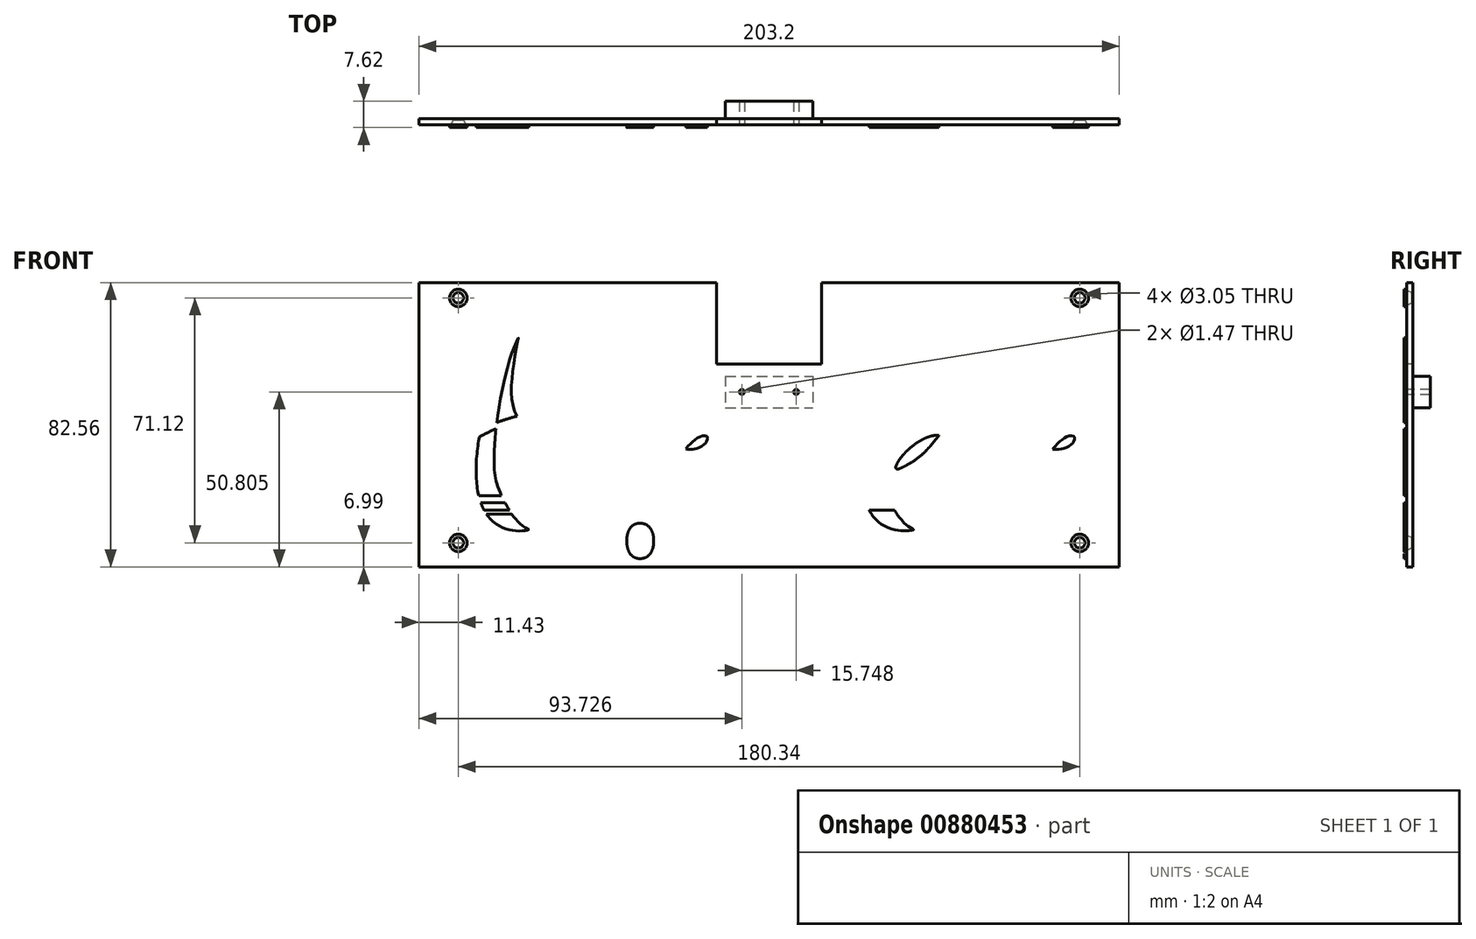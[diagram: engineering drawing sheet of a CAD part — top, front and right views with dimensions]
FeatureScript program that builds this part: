
annotation { "Feature Type Name" : "Feature", "Feature Type Description" : "" }
export const myFeature = defineFeature(function(context is Context, id is Id, definition is map)
    precondition{}
    {
        {
            var Q0;
            Q0=qCreatedBy(makeId("Front.planeOp"),FACE);
            var sketch = newSketch(context, id + "F0", { "sketchPlane" : qUnion([Q0])});
            skLineSegment(sketch, "E0.bottom", {"start": v(-101.6, 41.27) * mm, "end": v(101.6, 41.27) * mm});
            skLineSegment(sketch, "E0.top", {"start": v(-101.6, -41.27) * mm, "end": v(101.6, -41.27) * mm});
            skLineSegment(sketch, "E0.left", {"start": v(-101.6, 41.27) * mm, "end": v(-101.6, -41.27) * mm});
            skLineSegment(sketch, "E0.right", {"start": v(101.6, 41.27) * mm, "end": v(101.6, -41.27) * mm});
            skPoint(sketch, "E0.middle", {"position": v(0, 0) * mm});
            skSolve(sketch);
        }
        {
            var Q0;
            Q0 = qSketchRegion(id + "F0", true);
            extrude(context, id + "F1", {"entities" : qUnion([Q0]), "depth" : 2.54 * mm, "offsetDistance" : 25.4 * mm});
        }
        {
            var Q0;
            Q0=makeQuery(id+"F1.opExtrude","CAP_FACE",FACE,{"disambiguationData":[OSD([sQuery(id+"F0.wireOp",EDGE,"E0.bottom"),sQuery(id+"F0.wireOp",EDGE,"E0.top"),sQuery(id+"F0.wireOp",EDGE,"E0.left"),sQuery(id+"F0.wireOp",EDGE,"E0.right")])],"isStart":false});
            var sketch = newSketch(context, id + "F2", { "sketchPlane" : qUnion([Q0])});
            skLineSegment(sketch, "E1.bottom", {"start": v(-99.06, 41.27) * mm, "end": v(-82.55, 41.27) * mm});
            skLineSegment(sketch, "E1.top", {"start": v(-99.06, 32.38) * mm, "end": v(-82.55, 32.38) * mm});
            skLineSegment(sketch, "E1.left", {"start": v(-99.06, 41.27) * mm, "end": v(-99.06, 32.38) * mm});
            skLineSegment(sketch, "E1.right", {"start": v(-82.55, 41.27) * mm, "end": v(-82.55, 32.38) * mm});
            skLineSegment(sketch, "E2.bottom", {"start": v(99.06, 41.27) * mm, "end": v(82.55, 41.27) * mm});
            skLineSegment(sketch, "E2.top", {"start": v(99.06, 32.38) * mm, "end": v(82.55, 32.38) * mm});
            skLineSegment(sketch, "E2.left", {"start": v(99.06, 41.27) * mm, "end": v(99.06, 32.38) * mm});
            skLineSegment(sketch, "E2.right", {"start": v(82.55, 41.27) * mm, "end": v(82.55, 32.38) * mm});
            skLineSegment(sketch, "E3.bottom", {"start": v(99.06, -38.73) * mm, "end": v(82.55, -38.73) * mm});
            skLineSegment(sketch, "E3.top", {"start": v(99.06, -29.84) * mm, "end": v(82.55, -29.84) * mm});
            skLineSegment(sketch, "E3.left", {"start": v(99.06, -38.73) * mm, "end": v(99.06, -29.84) * mm});
            skLineSegment(sketch, "E3.right", {"start": v(82.55, -38.74) * mm, "end": v(82.55, -29.85) * mm});
            skLineSegment(sketch, "E4.bottom", {"start": v(-99.06, -38.74) * mm, "end": v(-82.55, -38.74) * mm});
            skLineSegment(sketch, "E4.top", {"start": v(-99.06, -29.85) * mm, "end": v(-82.55, -29.85) * mm});
            skLineSegment(sketch, "E4.left", {"start": v(-99.06, -38.74) * mm, "end": v(-99.06, -29.85) * mm});
            skLineSegment(sketch, "E4.right", {"start": v(-82.55, -38.74) * mm, "end": v(-82.55, -29.85) * mm});
            skPoint(sketch, "E5", {"position": v(-90.17, 36.83) * mm});
            skPoint(sketch, "E5.positionSnap0", {"position": v(-82.55, 36.83) * mm});
            skPoint(sketch, "E6", {"position": v(-90.17, -34.3) * mm});
            skPoint(sketch, "E6.positionSnap0", {"position": v(-82.55, -34.3) * mm});
            skPoint(sketch, "E7", {"position": v(90.17, -34.3) * mm});
            skPoint(sketch, "E8", {"position": v(90.17, 36.83) * mm});
            skPoint(sketch, "E8.positionSnap0", {"position": v(82.55, 36.83) * mm});
            skLineSegment(sketch, "E9.bottom", {"start": v(-15.24, 41.27) * mm, "end": v(15.24, 41.27) * mm});
            skLineSegment(sketch, "E9.top", {"start": v(-15.24, 17.65) * mm, "end": v(15.24, 17.65) * mm});
            skLineSegment(sketch, "E9.left", {"start": v(-15.24, 41.27) * mm, "end": v(-15.24, 17.65) * mm});
            skLineSegment(sketch, "E9.right", {"start": v(15.24, 41.27) * mm, "end": v(15.24, 17.65) * mm});
            skPoint(sketch, "E9.middle", {"position": v(0, 29.46) * mm});
            skLineSegment(sketch, "E10.bottom", {"start": v(-12.7, 17.65) * mm, "end": v(12.7, 17.65) * mm});
            skLineSegment(sketch, "E10.top", {"start": v(-12.7, 4.95) * mm, "end": v(12.7, 4.95) * mm});
            skLineSegment(sketch, "E10.left", {"start": v(-12.7, 17.65) * mm, "end": v(-12.7, 4.95) * mm});
            skLineSegment(sketch, "E10.right", {"start": v(12.7, 17.65) * mm, "end": v(12.7, 4.95) * mm});
            skPoint(sketch, "E10.middle", {"position": v(0, 11.3) * mm});
            skLineSegment(sketch, "E11", {"start": v(-12.7, 9.52) * mm, "end": v(12.7, 9.52) * mm, "construction": true});
            skPoint(sketch, "E12", {"position": v(0, 9.52) * mm});
            skPoint(sketch, "E13", {"position": v(-7.87, 9.52) * mm});
            skPoint(sketch, "E14", {"position": v(7.87, 9.52) * mm});
            skLineSegment(sketch, "E15", {"start": v(-12.7, 14.1) * mm, "end": v(12.7, 14.1) * mm});
            skSolve(sketch);
        }
        {
            var Q0;
            Q0=sQuery(id+"F2.wireOp",VERTEX,"E5");
            var Q1;
            Q1=sQuery(id+"F2.wireOp",VERTEX,"E6");
            var Q2;
            Q2=sQuery(id+"F2.wireOp",VERTEX,"E7");
            var Q3;
            Q3=sQuery(id+"F2.wireOp",VERTEX,"E8");
            var Q4;
            Q4=makeQuery(id+"F1.opExtrude","SWEPT_BODY",BODY,{"disambiguationData":[OSD([sQuery(id+"F0.wireOp",EDGE,"E0.bottom"),sQuery(id+"F0.wireOp",EDGE,"E0.top"),sQuery(id+"F0.wireOp",EDGE,"E0.left"),sQuery(id+"F0.wireOp",EDGE,"E0.right")])]});
            hole(context, id + "F3", {"style" : HoleStyle.C_SINK, "endStyle" : HoleEndStyle.THROUGH, "holeDiameter" : 3.05 * mm, "cSinkDiameter" : 5.08 * mm, "cSinkAngle" : 49 * degree, "majorDiameter" : 6.35 * mm, "isTappedThrough" : true, "tappedDepth" : 12.7 * mm, "tapClearance" : 3, "locations" : qUnion([Q0, Q1, Q2, Q3]), "scope" : qUnion([Q4])});
        }
        {
            var Q0;
            Q0=makeQuery(id+"F2.imprint","IMPRINT",FACE,{"disambiguationData":[TD([[makeQuery(id+"F2.imprint","IMPRINT",EDGE,{"derivedFrom":sQuery(id+"F2.wireOp",EDGE,"rZs2VQ7l-vhOc-SYSJ-Oo8c-zqr43qeV2ue8.bottom")}),-1.0]])]});
            var Q1;
            Q1=makeQuery(id+"F2.imprint","IMPRINT",FACE,{"disambiguationData":[TD([[makeQuery(id+"F2.imprint","IMPRINT",EDGE,{"derivedFrom":sQuery(id+"F2.wireOp",EDGE,"E9.bottom")}),-1.0]])]});
            extrude(context, id + "F4", {"entities" : qUnion([Q0, Q1]), "operationType" : NewBodyOperationType.REMOVE, "oppositeDirection" : true, "depth" : 25.4 * mm, "offsetDistance" : 25.4 * mm});
        }
        {
            var Q0;
            {var subQ0=sQuery(id+"F2.wireOp",EDGE,"E10.top");Q0=makeQuery(id+"F2.imprint","IMPRINT",FACE,{"disambiguationData":[TD([[makeQuery(id+"F2.imprint","IMPRINT",EDGE,{"derivedFrom":subQ0}),1.0]])]});}
            extrude(context, id + "F5", {"entities" : qUnion([Q0]), "operationType" : NewBodyOperationType.ADD, "oppositeDirection" : true, "depth" : 7.62 * mm, "offsetDistance" : 25.4 * mm});
        }
        {
            var Q0;
            Q0=sQuery(id+"F2.wireOp",VERTEX,"E13");
            var Q1;
            Q1=sQuery(id+"F2.wireOp",VERTEX,"E14");
            var Q2;
            Q2=makeQuery(id+"F1.opExtrude","SWEPT_BODY",BODY,{"disambiguationData":[OSD([sQuery(id+"F0.wireOp",EDGE,"E0.bottom"),sQuery(id+"F0.wireOp",EDGE,"E0.top"),sQuery(id+"F0.wireOp",EDGE,"E0.left"),sQuery(id+"F0.wireOp",EDGE,"E0.right")])]});
            hole(context, id + "F6", {"style" : HoleStyle.SIMPLE, "endStyle" : HoleEndStyle.BLIND, "holeDiameter" : 1.47 * mm, "majorDiameter" : 6.35 * mm, "holeDepth" : 10.16 * mm, "isTappedThrough" : true, "tappedDepth" : 12.7 * mm, "tapClearance" : 3, "locations" : qUnion([Q0, Q1]), "scope" : qUnion([Q2])});
        }
        {
            var Q0;
            Q0=makeQuery(id+"F1.opExtrude","CAP_FACE",FACE,{"disambiguationData":[OSD([sQuery(id+"F0.wireOp",EDGE,"E0.bottom"),sQuery(id+"F0.wireOp",EDGE,"E0.top"),sQuery(id+"F0.wireOp",EDGE,"E0.left"),sQuery(id+"F0.wireOp",EDGE,"E0.right")])],"isStart":false});
            var sketch = newSketch(context, id + "F7", { "sketchPlane" : qUnion([Q0])});
            skLineSegment(sketch, "E16.bottom", {"start": v(-99.39, -20.57) * mm, "end": v(98.42, -20.57) * mm});
            skLineSegment(sketch, "E16.top", {"start": v(-99.39, -22.6) * mm, "end": v(98.42, -22.6) * mm});
            skLineSegment(sketch, "E16.left", {"start": v(-99.39, -20.57) * mm, "end": v(-99.39, -22.6) * mm});
            skLineSegment(sketch, "E16.right", {"start": v(98.42, -20.57) * mm, "end": v(98.42, -22.6) * mm});
            skLineSegment(sketch, "E17.bottom", {"start": v(-99.39, -24.83) * mm, "end": v(98.42, -24.83) * mm});
            skLineSegment(sketch, "E17.top", {"start": v(-99.39, -25.88) * mm, "end": v(98.42, -25.88) * mm});
            skLineSegment(sketch, "E17.left", {"start": v(-99.39, -24.83) * mm, "end": v(-99.39, -25.88) * mm});
            skLineSegment(sketch, "E17.right", {"start": v(98.42, -24.83) * mm, "end": v(98.42, -25.88) * mm});
            skFitSpline(sketch, "E18", {"points": [v(-99.39, -13.37) * mm, v(-98.49, -14.18) * mm, v(-98.4, -14.28) * mm, v(-98.28, -14.17) * mm, v(-96.93, -12.76) * mm, v(-95.43, -11.38) * mm, v(-93.7, -9.92) * mm, v(-91.22, -7.99) * mm, v(-88.97, -6.44) * mm, v(-86.37, -4.82) * mm, v(-84.08, -3.54) * mm, v(-79.14, -1.1) * mm, v(-76.01, 0.1) * mm, v(-72.39, 1.31) * mm, v(-68.08, 2.4) * mm, v(-64.6, 3.07) * mm, v(-61.72, 3.46) * mm, v(-58.9, 3.7) * mm, v(-56.18, 3.84) * mm, v(-52.18, 3.75) * mm, v(-47.22, 3.4) * mm, v(-44.4, 3) * mm, v(-41.38, 2.42) * mm, v(-39.4, 2) * mm, v(-39.54, 2.08) * mm, v(-40.44, 2.32) * mm, v(-42.26, 2.75) * mm, v(-45.54, 3.4) * mm, v(-47.8, 3.78) * mm, v(-50.36, 4.1) * mm, v(-52.71, 4.33) * mm, v(-55.15, 4.46) * mm, v(-57.94, 4.5) * mm, v(-60.7, 4.44) * mm, v(-63.58, 4.22) * mm, v(-67, 3.8) * mm, v(-69.33, 3.38) * mm, v(-71.76, 2.87) * mm, v(-74.4, 2.15) * mm, v(-76.35, 1.56) * mm, v(-78, 1.02) * mm, v(-79, 0.66) * mm, v(-83.6, -1.22) * mm, v(-86.89, -2.84) * mm, v(-89.86, -4.53) * mm, v(-92.19, -5.98) * mm, v(-94.38, -7.5) * mm, v(-96.5, -9.12) * mm, v(-98.21, -10.58) * mm, v(-99.5, -11.75) * mm, v(-100.21, -12.45) * mm, v(-100.24, -12.51) * mm, v(-100.18, -12.6) * mm, v(-99.72, -13.04) * mm, v(-99.39, -13.37) * mm]});
            skFitSpline(sketch, "E19", {"points": [v(-69.85, -30.36) * mm, v(-69.72, -30.45) * mm, v(-69.94, -30.55) * mm, v(-70.41, -30.65) * mm, v(-70.92, -30.73) * mm, v(-71.77, -30.84) * mm, v(-72.94, -30.84) * mm, v(-74.08, -30.7) * mm, v(-75.15, -30.53) * mm, v(-76.3, -30.22) * mm, v(-77.61, -29.7) * mm, v(-78.84, -29.04) * mm, v(-80.19, -28.03) * mm, v(-81.17, -27.03) * mm, v(-81.85, -26.16) * mm, v(-82.41, -25.28) * mm, v(-82.99, -24.23) * mm, v(-83.45, -23.13) * mm, v(-83.94, -21.79) * mm, v(-84.38, -19.96) * mm, v(-84.73, -17.88) * mm, v(-84.92, -15.83) * mm, v(-85, -13.09) * mm, v(-84.91, -10.36) * mm, v(-84.7, -7.94) * mm, v(-84.4, -5.56) * mm, v(-84.13, -3.82) * mm, v(-83.72, -1.92) * mm, v(-83.24, 0.53) * mm, v(-82.35, 3.98) * mm, v(-81.4, 7.25) * mm, v(-80.28, 10.95) * mm, v(-78.6, 15.64) * mm, v(-76.82, 20.12) * mm, v(-75.21, 23.83) * mm, v(-73.83, 26.82) * mm, v(-72.43, 29.66) * mm, v(-71.33, 31.65) * mm, v(-71.2, 31.83) * mm, v(-70.88, 31.85) * mm, v(-70.46, 31.82) * mm, v(-69.92, 31.64) * mm, v(-69.72, 31.52) * mm, v(-69.77, 31.22) * mm, v(-70.28, 29.04) * mm, v(-70.9, 26.38) * mm, v(-71.46, 23.53) * mm, v(-72.11, 19.9) * mm, v(-72.62, 16.3) * mm, v(-72.96, 13.2) * mm, v(-73.13, 11.06) * mm, v(-73.2, 8.7) * mm, v(-72.96, 6.27) * mm, v(-72.39, 4.05) * mm, v(-72.03, 3.01) * mm, v(-71.55, 2.04) * mm, v(-71.01, 1.27) * mm, v(-70.16, 0.39) * mm, v(-69.38, -0.13) * mm, v(-68.74, -0.5) * mm, v(-68.6, -0.57) * mm, v(-68.78, -0.6) * mm, v(-69.3, -0.6) * mm, v(-69.86, -0.5) * mm, v(-70.5, -0.21) * mm, v(-71.05, 0.16) * mm, v(-71.83, 0.81) * mm, v(-72.16, 1.17) * mm, v(-72.64, 1.79) * mm, v(-73.15, 2.6) * mm, v(-73.8, 3.88) * mm, v(-74.19, 5.1) * mm, v(-74.56, 6.8) * mm, v(-74.73, 8.53) * mm, v(-74.78, 10.39) * mm, v(-74.68, 12.54) * mm, v(-74.5, 14.34) * mm, v(-74.2, 16.97) * mm, v(-73.87, 19.16) * mm, v(-73.45, 21.5) * mm, v(-73.03, 23.66) * mm, v(-72.73, 25.04) * mm, v(-72.7, 25.22) * mm, v(-72.86, 25.01) * mm, v(-73.28, 24.03) * mm, v(-74.08, 22.26) * mm, v(-74.63, 21) * mm, v(-75.1, 19.38) * mm, v(-75.94, 16.33) * mm, v(-76.99, 12.07) * mm, v(-77.88, 7.83) * mm, v(-78.47, 4.47) * mm, v(-78.84, 1.84) * mm, v(-79.1, 0.05) * mm, v(-79.33, -1.92) * mm, v(-79.51, -4.07) * mm, v(-79.7, -7.13) * mm, v(-79.79, -9.63) * mm, v(-79.79, -12.03) * mm, v(-79.54, -14.42) * mm, v(-79.14, -16.53) * mm, v(-78.2, -19.32) * mm, v(-77.03, -21.86) * mm, v(-75.64, -24.3) * mm, v(-74.49, -26.1) * mm, v(-73.94, -26.87) * mm, v(-73.18, -27.76) * mm, v(-72.52, -28.47) * mm, v(-71.59, -29.32) * mm, v(-70.71, -29.93) * mm, v(-70.12, -30.24) * mm, v(-69.85, -30.36) * mm]});
            skFitSpline(sketch, "E20", {"points": [v(41.78, -30.33) * mm, v(42.01, -30.45) * mm, v(41.87, -30.52) * mm, v(41.45, -30.64) * mm, v(40.67, -30.74) * mm, v(39.96, -30.8) * mm, v(39.22, -30.81) * mm, v(38.16, -30.78) * mm, v(37.1, -30.63) * mm, v(35.95, -30.38) * mm, v(34.5, -29.89) * mm, v(32.96, -29.07) * mm, v(31.8, -28.25) * mm, v(30.75, -27.2) * mm, v(29.85, -26.09) * mm, v(29.32, -25.23) * mm, v(28.77, -24.25) * mm, v(28.19, -22.93) * mm, v(27.75, -21.63) * mm, v(27.3, -19.79) * mm, v(27.06, -18.22) * mm, v(26.84, -16.17) * mm, v(26.75, -14.13) * mm, v(26.75, -11.98) * mm, v(26.84, -10) * mm, v(27.06, -7.76) * mm, v(27.38, -5.27) * mm, v(27.79, -2.84) * mm, v(28.33, -0.38) * mm, v(28.9, 2.15) * mm, v(29.9, 5.76) * mm, v(31.53, 11.05) * mm, v(33, 15.33) * mm, v(34.8, 19.85) * mm, v(36.6, 24.06) * mm, v(38.29, 27.6) * mm, v(40.44, 31.72) * mm, v(40.53, 31.84) * mm, v(40.75, 31.9) * mm, v(41.11, 31.84) * mm, v(41.55, 31.73) * mm, v(41.98, 31.5) * mm, v(42.03, 31.46) * mm, v(41.95, 31.3) * mm, v(41.08, 29.61) * mm, v(40.26, 27.95) * mm, v(39.36, 26.06) * mm, v(37.5, 21.88) * mm, v(37.02, 20.76) * mm, v(35.83, 16.46) * mm, v(34.55, 11.25) * mm, v(33.75, 7.34) * mm, v(32.83, 1.74) * mm, v(32.4, -2.34) * mm, v(32.01, -6.96) * mm, v(31.94, -9.98) * mm, v(32.1, -13.2) * mm, v(32.48, -15.89) * mm, v(33.23, -18.56) * mm, v(34.02, -20.36) * mm, v(34.8, -21.88) * mm, v(35.87, -23.96) * mm, v(37.3, -26.14) * mm, v(38.22, -27.37) * mm, v(39.27, -28.52) * mm, v(40, -29.23) * mm, v(40.56, -29.65) * mm, v(41.11, -30) * mm, v(41.78, -30.33) * mm]});
            skFitSpline(sketch, "E21", {"points": [v(-77.34, -13.2) * mm, v(-77.53, -12.77) * mm, v(-77.62, -12.5) * mm, v(-77.54, -12.07) * mm, v(-77.01, -11.44) * mm, v(-75.8, -10.4) * mm, v(-75.03, -9.75) * mm, v(-74.83, -9.6) * mm, v(-73.77, -8.2) * mm, v(-71.45, -4.88) * mm, v(-70.26, -3.1) * mm, v(-69.98, -2.85) * mm, v(-69.54, -2.8) * mm, v(-69, -2.94) * mm, v(-68.48, -3.33) * mm, v(-68.44, -3.72) * mm, v(-68.68, -4.1) * mm, v(-70.07, -5.64) * mm, v(-70.96, -6.84) * mm, v(-71.37, -7.37) * mm, v(-71.5, -7.58) * mm, v(-71.2, -7.47) * mm, v(-70.86, -7.23) * mm, v(-68.87, -6.07) * mm, v(-67.23, -5.13) * mm, v(-64.84, -3.82) * mm, v(-62.8, -2.83) * mm, v(-61.57, -2.35) * mm, v(-61, -2.32) * mm, v(-60.6, -2.61) * mm, v(-60.4, -2.99) * mm, v(-60.58, -3.33) * mm, v(-61, -3.83) * mm, v(-61.98, -4.8) * mm, v(-63.5, -6.42) * mm, v(-64.58, -7.67) * mm, v(-65.75, -9.14) * mm, v(-66.83, -10.76) * mm, v(-67.34, -11.81) * mm, v(-67.46, -12.5) * mm, v(-67.32, -13.07) * mm, v(-66.74, -13.42) * mm, v(-65.92, -13.48) * mm, v(-64.01, -13.2) * mm, v(-61.05, -12) * mm, v(-58.33, -10.55) * mm, v(-57.1, -9.75) * mm, v(-55.38, -8.53) * mm, v(-55.05, -8.32) * mm, v(-55.6, -9.43) * mm, v(-56.18, -9.65) * mm, v(-56.63, -9.87) * mm, v(-57.53, -10.48) * mm, v(-58.37, -11.01) * mm, v(-59.95, -11.92) * mm, v(-61.58, -12.69) * mm, v(-63.45, -13.4) * mm, v(-65.27, -13.9) * mm, v(-66.76, -14.12) * mm, v(-68.4, -14.12) * mm, v(-69.33, -13.96) * mm, v(-69.81, -13.74) * mm, v(-70.04, -13.26) * mm, v(-69.92, -12.5) * mm, v(-69.4, -11.45) * mm, v(-67.66, -9.18) * mm, v(-65.97, -7.16) * mm, v(-64.92, -5.92) * mm, v(-64.04, -4.74) * mm, v(-63.77, -4.17) * mm, v(-63.95, -3.95) * mm, v(-64.34, -4.04) * mm, v(-65.94, -4.84) * mm, v(-69.02, -6.6) * mm, v(-71.16, -7.98) * mm, v(-71.95, -8.55) * mm, v(-72.65, -9.2) * mm, v(-73.73, -10.43) * mm, v(-74.95, -11.87) * mm, v(-75.92, -12.96) * mm, v(-76.6, -13.62) * mm, v(-76.92, -13.68) * mm, v(-77.2, -13.5) * mm, v(-77.34, -13.2) * mm]});
            skFitSpline(sketch, "E22", {"points": [v(-45.1, -5.77) * mm, v(-45.2, -6) * mm, v(-44.96, -6.03) * mm, v(-44.25, -5.67) * mm, v(-43.46, -5.18) * mm, v(-43.1, -4.6) * mm, v(-43.05, -3.91) * mm, v(-43.43, -3.21) * mm, v(-44.33, -2.81) * mm, v(-45.5, -2.67) * mm, v(-46.88, -2.81) * mm, v(-48.87, -3.5) * mm, v(-50.67, -4.32) * mm, v(-52.34, -5.33) * mm, v(-53.65, -6.34) * mm, v(-54.84, -7.47) * mm, v(-55.5, -8.23) * mm, v(-55.91, -8.79) * mm, v(-56.45, -9.56) * mm, v(-56.78, -10.3) * mm, v(-57.02, -11.04) * mm, v(-57.06, -11.84) * mm, v(-56.86, -12.53) * mm, v(-56.36, -13.1) * mm, v(-55.6, -13.47) * mm, v(-54.41, -13.77) * mm, v(-52.9, -13.83) * mm, v(-51.33, -13.73) * mm, v(-49.3, -13.27) * mm, v(-47.12, -12.5) * mm, v(-44.79, -11.41) * mm, v(-41.78, -9.57) * mm, v(-39.31, -7.84) * mm, v(-38.14, -7) * mm, v(-37.84, -6.7) * mm, v(-37.93, -6.5) * mm, v(-38.42, -6.57) * mm, v(-38.75, -6.84) * mm, v(-39.98, -7.77) * mm, v(-41.5, -8.9) * mm, v(-43.3, -10.06) * mm, v(-44.77, -10.9) * mm, v(-46.71, -11.8) * mm, v(-48.57, -12.54) * mm, v(-50.37, -13.02) * mm, v(-52.07, -13.07) * mm, v(-53.32, -12.67) * mm, v(-54.12, -11.89) * mm, v(-54.25, -10.7) * mm, v(-54.08, -9.56) * mm, v(-53.56, -8.1) * mm, v(-52.72, -6.76) * mm, v(-51.58, -5.55) * mm, v(-50.45, -4.74) * mm, v(-49.04, -4.12) * mm, v(-47.7, -3.86) * mm, v(-46.31, -3.93) * mm, v(-45.54, -4.3) * mm, v(-45.08, -4.85) * mm, v(-45.1, -5.77) * mm]});
            skFitSpline(sketch, "E23", {"points": [v(-33.43, -3.72) * mm, v(-33.26, -3.56) * mm, v(-33.06, -3.13) * mm, v(-33.16, -3.03) * mm, v(-33.44, -3) * mm, v(-34.05, -3.1) * mm, v(-35.07, -3.4) * mm, v(-35.43, -3.53) * mm, v(-35.62, -3.6) * mm, v(-35.98, -3.92) * mm, v(-37.4, -5.44) * mm, v(-38.24, -6.35) * mm, v(-39.94, -8.42) * mm, v(-40.66, -9.4) * mm, v(-41.4, -10.53) * mm, v(-41.77, -11.37) * mm, v(-41.78, -12.32) * mm, v(-41.32, -12.87) * mm, v(-40.47, -13.32) * mm, v(-39.31, -13.48) * mm, v(-37.66, -13.47) * mm, v(-35.8, -13.16) * mm, v(-33.52, -12.46) * mm, v(-31.34, -11.43) * mm, v(-28.7, -9.95) * mm, v(-26.52, -8.45) * mm, v(-26.38, -8.32) * mm, v(-26.68, -8.43) * mm, v(-27.3, -8.65) * mm, v(-27.83, -8.93) * mm, v(-28.59, -9.42) * mm, v(-30.11, -10.33) * mm, v(-32.2, -11.41) * mm, v(-34.12, -12.23) * mm, v(-35.79, -12.7) * mm, v(-37.32, -12.83) * mm, v(-38.42, -12.54) * mm, v(-38.84, -11.93) * mm, v(-38.63, -10.76) * mm, v(-37.74, -9.12) * mm, v(-36.31, -7.08) * mm, v(-34.58, -5) * mm, v(-33.43, -3.72) * mm]});
            skFitSpline(sketch, "E24", {"points": [v(-30.4, 4.17) * mm, v(-30, 4.35) * mm, v(-29.4, 4.52) * mm, v(-28.83, 4.53) * mm, v(-28.35, 4.44) * mm, v(-28.14, 4.22) * mm, v(-28.06, 3.85) * mm, v(-28.15, 3.53) * mm, v(-28.47, 3.05) * mm, v(-28.52, 3) * mm, v(-29, 2.58) * mm, v(-29.04, 2.56) * mm, v(-29.53, 2.31) * mm, v(-29.6, 2.28) * mm, v(-30.2, 2.14) * mm, v(-30.8, 2.16) * mm, v(-31.21, 2.3) * mm, v(-31.38, 2.61) * mm, v(-31.33, 3.02) * mm, v(-31.19, 3.37) * mm, v(-30.97, 3.67) * mm, v(-30.62, 4.02) * mm, v(-30.4, 4.17) * mm]});
            skFitSpline(sketch, "E25", {"points": [v(-24.17, -7.05) * mm, v(-23.92, -6.7) * mm, v(-23.16, -5.85) * mm, v(-21.9, -4.66) * mm, v(-20.42, -3.62) * mm, v(-19.14, -3.2) * mm, v(-18.3, -3.23) * mm, v(-17.91, -3.57) * mm, v(-17.9, -4.05) * mm, v(-18.05, -4.72) * mm, v(-18.48, -5.36) * mm, v(-19.33, -6.08) * mm, v(-20.47, -6.7) * mm, v(-21.42, -7) * mm, v(-22.29, -7.14) * mm, v(-23.47, -7.18) * mm, v(-24.17, -7.05) * mm]});
            skFitSpline(sketch, "E26", {"points": [v(-24.52, -7.58) * mm, v(-24.33, -7.59) * mm, v(-22.9, -7.58) * mm, v(-19.62, -7) * mm, v(-17.33, -5.96) * mm, v(-15.87, -4.57) * mm, v(-15.5, -3.6) * mm, v(-15.85, -2.95) * mm, v(-16.86, -2.65) * mm, v(-18.48, -2.7) * mm, v(-20.68, -3.33) * mm, v(-23.37, -4.7) * mm, v(-25.9, -6.67) * mm, v(-27.47, -8.55) * mm, v(-28.4, -10.3) * mm, v(-28.7, -11.58) * mm, v(-28.46, -12.77) * mm, v(-27.2, -13.67) * mm, v(-25.78, -13.9) * mm, v(-23.09, -13.77) * mm, v(-20.54, -13.21) * mm, v(-17.52, -12.15) * mm, v(-14.42, -10.63) * mm, v(-10.85, -8.25) * mm, v(-10.75, -8.16) * mm, v(-10.54, -7.63) * mm, v(-10.78, -7.63) * mm, v(-11.45, -8.07) * mm, v(-12.74, -9.04) * mm, v(-15.12, -10.48) * mm, v(-17.29, -11.54) * mm, v(-19.65, -12.4) * mm, v(-21.63, -12.85) * mm, v(-23.67, -12.89) * mm, v(-25.2, -12.34) * mm, v(-25.68, -11.21) * mm, v(-25.62, -10.03) * mm, v(-25.16, -8.7) * mm, v(-24.6, -7.7) * mm, v(-24.52, -7.58) * mm]});
            skFitSpline(sketch, "E27", {"points": [v(-8.84, -7.46) * mm, v(-9.05, -7.58) * mm, v(-9, -7.4) * mm, v(-8.36, -6.57) * mm, v(-7.25, -5.22) * mm, v(-6.24, -4.06) * mm, v(-6.03, -3.76) * mm, v(-6, -3.42) * mm, v(-6.35, -3.08) * mm, v(-6.75, -2.85) * mm, v(-7.36, -2.84) * mm, v(-7.68, -2.9) * mm, v(-7.95, -3.21) * mm, v(-8.41, -3.93) * mm, v(-9.3, -5.23) * mm, v(-10.43, -6.81) * mm, v(-10.87, -7.46) * mm, v(-12.14, -9.24) * mm, v(-12.27, -9.44) * mm, v(-12.66, -9.79) * mm, v(-13.7, -10.65) * mm, v(-14.65, -11.47) * mm, v(-15.1, -11.96) * mm, v(-15.25, -12.33) * mm, v(-15.16, -12.8) * mm, v(-14.8, -13.46) * mm, v(-14.48, -13.69) * mm, v(-14.14, -13.63) * mm, v(-12.7, -12.08) * mm, v(-11.24, -10.36) * mm, v(-9.77, -8.72) * mm, v(-9.62, -8.59) * mm, v(-8.5, -7.8) * mm, v(-5.81, -6.13) * mm, v(-2.63, -4.38) * mm, v(-1.82, -4) * mm, v(-1.45, -4.02) * mm, v(-1.4, -4.26) * mm, v(-1.55, -4.54) * mm, v(-2.5, -5.85) * mm, v(-4.1, -7.74) * mm, v(-5.67, -9.62) * mm, v(-6.78, -11.12) * mm, v(-7.49, -12.38) * mm, v(-7.65, -13.3) * mm, v(-7.32, -13.84) * mm, v(-6.35, -14.1) * mm, v(-4.92, -14.17) * mm, v(-3.5, -14.06) * mm, v(-0.99, -13.43) * mm, v(1.88, -12.24) * mm, v(4.5, -10.8) * mm, v(6.93, -9.06) * mm, v(7.85, -8.4) * mm, v(8.1, -8.1) * mm, v(7.82, -8.11) * mm, v(7.33, -8.32) * mm, v(6.94, -8.53) * mm, v(5.21, -9.76) * mm, v(3.55, -10.79) * mm, v(1.46, -11.87) * mm, v(-1.26, -13.04) * mm, v(-2.56, -13.4) * mm, v(-4.09, -13.47) * mm, v(-4.88, -13.1) * mm, v(-5.05, -12.3) * mm, v(-4.5, -10.89) * mm, v(-2.63, -8.2) * mm, v(-0.48, -5.76) * mm, v(1.47, -3.74) * mm, v(1.95, -3.13) * mm, v(1.98, -2.83) * mm, v(1.58, -2.44) * mm, v(1.05, -2.3) * mm, v(0.4, -2.48) * mm, v(-2.34, -3.74) * mm, v(-4.74, -5.03) * mm, v(-6.83, -6.22) * mm, v(-8.16, -7.02) * mm, v(-8.84, -7.46) * mm]});
            skFitSpline(sketch, "E28", {"points": [v(17.04, 3.06) * mm, v(17.32, 3.34) * mm, v(17.46, 3.5) * mm, v(17.8, 3.6) * mm, v(21.94, 4.76) * mm, v(22.15, 4.81) * mm, v(22.41, 4.75) * mm, v(22.41, 4.56) * mm, v(22.18, 4.4) * mm, v(21.69, 4.3) * mm, v(20.8, 4.04) * mm, v(20.18, 3.7) * mm, v(19.49, 3.08) * mm, v(17.6, 1.19) * mm, v(15.82, -0.77) * mm, v(14.1, -2.74) * mm, v(12.33, -4.83) * mm, v(10.04, -7.9) * mm, v(8.99, -9.96) * mm, v(8.8, -11.14) * mm, v(9.06, -12.17) * mm, v(9.97, -12.7) * mm, v(11.02, -12.9) * mm, v(12.6, -12.74) * mm, v(14.66, -12.21) * mm, v(16.14, -11.68) * mm, v(16.96, -11.36) * mm, v(17.12, -11.3) * mm, v(17.38, -11.36) * mm, v(17.48, -11.6) * mm, v(17.37, -11.67) * mm, v(16.23, -12.14) * mm, v(14.56, -12.75) * mm, v(12.57, -13.33) * mm, v(10.14, -13.71) * mm, v(8.33, -13.77) * mm, v(6.92, -13.59) * mm, v(5.8, -12.88) * mm, v(5.44, -11.84) * mm, v(5.81, -10.42) * mm, v(6.13, -9.8) * mm, v(7.26, -8.07) * mm, v(8.53, -6.45) * mm, v(10.03, -4.7) * mm, v(12.06, -2.4) * mm, v(14.67, 0.57) * mm, v(17.04, 3.06) * mm]});
            skFitSpline(sketch, "E29", {"points": [v(7.9, -3.37) * mm, v(7.6, -3.37) * mm, v(7.41, -3.47) * mm, v(7, -3.75) * mm, v(6.7, -4.01) * mm, v(6.68, -4.12) * mm, v(6.8, -4.23) * mm, v(7.1, -4.25) * mm, v(10.11, -4.12) * mm, v(16.43, -3.85) * mm, v(22.48, -3.7) * mm, v(22.65, -3.68) * mm, v(22.8, -3.5) * mm, v(22.6, -3.3) * mm, v(22.43, -3.3) * mm, v(17.55, -3.3) * mm, v(13.79, -3.3) * mm, v(10.01, -3.31) * mm, v(7.9, -3.37) * mm]});
            skFitSpline(sketch, "E30", {"points": [v(52.67, -1.35) * mm, v(53.02, -1.3) * mm, v(52.87, -1.55) * mm, v(52.4, -2) * mm, v(51.82, -2.64) * mm, v(50.57, -4.1) * mm, v(48.01, -7.37) * mm, v(46.03, -10.21) * mm, v(45.11, -12.09) * mm, v(44.96, -12.98) * mm, v(45.25, -13.6) * mm, v(46.7, -13.87) * mm, v(48.58, -13.6) * mm, v(52.22, -12.05) * mm, v(55.35, -10.18) * mm, v(58.64, -7.92) * mm, v(58.88, -7.82) * mm, v(58.52, -8.44) * mm, v(57.8, -8.95) * mm, v(56.89, -9.57) * mm, v(54.33, -11.3) * mm, v(52.23, -12.48) * mm, v(49.62, -13.69) * mm, v(47.53, -14.34) * mm, v(46.11, -14.58) * mm, v(44.62, -14.62) * mm, v(43.7, -14.44) * mm, v(42.84, -13.77) * mm, v(42.6, -12.92) * mm, v(42.8, -11.88) * mm, v(43.4, -10.63) * mm, v(44.2, -9.55) * mm, v(45.76, -7.73) * mm, v(47.2, -5.68) * mm, v(48.71, -3.82) * mm, v(49.95, -2.3) * mm, v(50.31, -1.97) * mm, v(50.74, -1.7) * mm, v(52.67, -1.35) * mm]});
            skFitSpline(sketch, "E31", {"points": [v(53.63, -2.83) * mm, v(53.97, -2.88) * mm, v(54.25, -3.06) * mm, v(54.15, -3.3) * mm, v(53.71, -3.22) * mm, v(52.85, -3.15) * mm, v(51.72, -3.1) * mm, v(48.71, -3.06) * mm, v(46.54, -3.44) * mm, v(44.77, -4.16) * mm, v(42.89, -5.28) * mm, v(40.78, -6.88) * mm, v(39.3, -8.33) * mm, v(37.92, -10.04) * mm, v(37.1, -11.42) * mm, v(36.8, -12.3) * mm, v(36.9, -12.77) * mm, v(37.6, -12.8) * mm, v(39.27, -12.1) * mm, v(41.58, -10.78) * mm, v(43.75, -9.2) * mm, v(45.29, -7.78) * mm, v(48.5, -4.21) * mm, v(48.63, -4.03) * mm, v(46.34, -7.75) * mm, v(45.74, -8.05) * mm, v(44.58, -8.96) * mm, v(43.06, -10.23) * mm, v(41.29, -11.46) * mm, v(39.86, -12.32) * mm, v(37.96, -13.23) * mm, v(36.08, -13.81) * mm, v(34.66, -13.75) * mm, v(34.12, -13.43) * mm, v(33.9, -12.9) * mm, v(33.93, -12.33) * mm, v(34.63, -10.68) * mm, v(35.76, -9.22) * mm, v(37, -7.94) * mm, v(39.01, -6.36) * mm, v(41.79, -4.7) * mm, v(44.64, -3.48) * mm, v(46.86, -2.9) * mm, v(48.93, -2.66) * mm, v(52.25, -2.72) * mm, v(53.63, -2.83) * mm]});
            skFitSpline(sketch, "E32", {"points": [v(66.78, -4.6) * mm, v(67.03, -4.57) * mm, v(67.15, -4.64) * mm, v(67.12, -4.87) * mm, v(67.23, -6.15) * mm, v(67.9, -8.43) * mm, v(68.76, -10.4) * mm, v(69.59, -11.64) * mm, v(70.15, -12.1) * mm, v(71.41, -12.49) * mm, v(72.9, -12.4) * mm, v(74.78, -11.72) * mm, v(76.98, -10.45) * mm, v(78.63, -9.3) * mm, v(79.43, -8.7) * mm, v(79.55, -8.61) * mm, v(79.8, -9.3) * mm, v(78.72, -9.7) * mm, v(78.27, -10.02) * mm, v(77.53, -10.59) * mm, v(75.86, -11.68) * mm, v(74.16, -12.62) * mm, v(72.68, -13.26) * mm, v(71.55, -13.57) * mm, v(70.35, -13.79) * mm, v(68.69, -13.68) * mm, v(67.75, -13.25) * mm, v(67.06, -12.63) * mm, v(66.3, -11.3) * mm, v(65.58, -9.36) * mm, v(64.97, -7.31) * mm, v(64.68, -6.33) * mm, v(64.66, -5.68) * mm, v(64.85, -5.4) * mm, v(65.7, -4.96) * mm, v(66.78, -4.6) * mm]});
            skFitSpline(sketch, "E33", {"points": [v(59.2, -9.41) * mm, v(58.87, -9.9) * mm, v(58.8, -10.05) * mm, v(58.95, -10.03) * mm, v(59.42, -9.72) * mm, v(62.25, -7.9) * mm, v(64.34, -6.63) * mm, v(68.53, -4.2) * mm, v(72.2, -2.15) * mm, v(75.46, -0.48) * mm, v(75.94, -0.32) * mm, v(76.34, -0.32) * mm, v(76.83, -0.92) * mm, v(76.8, -1.14) * mm, v(76.66, -1.26) * mm, v(76, -1.43) * mm, v(74.55, -1.92) * mm, v(73.17, -2.48) * mm, v(70.78, -3.62) * mm, v(68.28, -4.96) * mm, v(64.62, -7.13) * mm, v(62.24, -8.72) * mm, v(60.16, -10.15) * mm, v(58.5, -11.45) * mm, v(57.34, -12.54) * mm, v(56.26, -13.75) * mm, v(56.17, -13.83) * mm, v(55.78, -13.9) * mm, v(55.19, -13.74) * mm, v(54.8, -13.26) * mm, v(54.67, -13) * mm, v(54.65, -12.42) * mm, v(54.66, -12.3) * mm, v(54.95, -12.02) * mm, v(56.37, -10.39) * mm, v(56.96, -9.62) * mm, v(58.78, -7.42) * mm, v(61.12, -4.66) * mm, v(67.4, 2.23) * mm, v(75.39, 9.85) * mm, v(79.06, 12.72) * mm, v(82.8, 15.05) * mm, v(86.6, 16.79) * mm, v(89.52, 17.44) * mm, v(92.21, 17.77) * mm, v(94.63, 17.32) * mm, v(95.62, 16.73) * mm, v(96, 15.92) * mm, v(95.86, 15.05) * mm, v(95.38, 14.4) * mm, v(95.04, 13.45) * mm, v(95.03, 13.3) * mm, v(94.77, 13.2) * mm, v(94.5, 13.31) * mm, v(94.55, 13.63) * mm, v(94.68, 14.04) * mm, v(94.42, 14.78) * mm, v(93.39, 15.6) * mm, v(91.59, 16.1) * mm, v(88.71, 16.16) * mm, v(86.08, 15.65) * mm, v(84.18, 15.06) * mm, v(81.83, 13.84) * mm, v(78.37, 11.4) * mm, v(72.77, 6.27) * mm, v(67.4, 0.31) * mm, v(63.5, -4.27) * mm, v(59.2, -9.41) * mm]});
            skFitSpline(sketch, "E34", {"points": [v(82.35, -7.1) * mm, v(82.42, -6.98) * mm, v(83.14, -6.13) * mm, v(84.48, -4.83) * mm, v(85.67, -3.94) * mm, v(86.87, -3.3) * mm, v(87.9, -3.2) * mm, v(88.53, -3.39) * mm, v(88.7, -3.9) * mm, v(88.49, -4.79) * mm, v(88.03, -5.43) * mm, v(87.22, -6.07) * mm, v(85.97, -6.72) * mm, v(84.87, -7.02) * mm, v(83.72, -7.15) * mm, v(83.04, -7.19) * mm, v(82.35, -7.1) * mm]});
            skFitSpline(sketch, "E35", {"points": [v(82.05, -7.59) * mm, v(82.34, -7.6) * mm, v(84.8, -7.47) * mm, v(87.3, -6.85) * mm, v(89.72, -5.63) * mm, v(90.89, -4.21) * mm, v(91, -3.38) * mm, v(90.5, -2.88) * mm, v(89.33, -2.64) * mm, v(87.72, -2.77) * mm, v(85.7, -3.41) * mm, v(83.35, -4.62) * mm, v(81.62, -5.85) * mm, v(79.97, -7.44) * mm, v(78.82, -9) * mm, v(78.1, -10.5) * mm, v(77.91, -11.95) * mm, v(78.12, -12.78) * mm, v(78.53, -13.2) * mm, v(79.43, -13.68) * mm, v(81.74, -13.9) * mm, v(85, -13.5) * mm, v(88.61, -12.31) * mm, v(91.87, -10.75) * mm, v(94.94, -8.8) * mm, v(96.28, -7.72) * mm, v(96.36, -7.64) * mm, v(96.22, -7.44) * mm, v(95.95, -7.4) * mm, v(95.65, -7.62) * mm, v(94.52, -8.51) * mm, v(92.48, -9.89) * mm, v(90, -11.2) * mm, v(87.46, -12.21) * mm, v(84.92, -12.85) * mm, v(82.88, -12.93) * mm, v(81.53, -12.46) * mm, v(80.96, -11.67) * mm, v(80.88, -10.41) * mm, v(81.1, -9.46) * mm, v(81.61, -8.3) * mm, v(81.92, -7.8) * mm, v(82.05, -7.59) * mm]});
            skText(sketch, "E36", { "text": "FOSSILS       INC", "fontName": "RobotoSlab-Regular.ttf"});
            skFitSpline(sketch, "E37", {"points": [v(49.33, -3.04) * mm, v(47.61, -3.18) * mm, v(44.58, -4.26) * mm, v(41.62, -6.2) * mm, v(38.76, -8.96) * mm, v(36.95, -11.74) * mm, v(36.8, -12.57) * mm, v(37.24, -12.85) * mm, v(38.67, -12.4) * mm, v(42.65, -10.04) * mm, v(45.73, -7.32) * mm, v(47.87, -4.99) * mm, v(48.07, -4.75) * mm, v(49.05, -4.94) * mm, v(50.3, -3.67) * mm, v(50.07, -3.16) * mm, v(49.33, -3.04) * mm]});
            const initialGuessF7  = {"E36": [-0.05484, -0.0401, 1, 0, 0.0129]};
            skSetInitialGuess(sketch, initialGuessF7);
            skSolve(sketch);
        }
        {
            var Q0;
            Q0=makeQuery(id+"F7.imprint","IMPRINT",FACE,{"disambiguationData":[TD([[makeQuery(id+"F7.imprint","IMPRINT",EDGE,{"derivedFrom":sQuery(id+"F7.wireOp",EDGE,"E36.sketch_text.stroke-0")}),-1.0]])]});
            var Q1;
            Q1=makeQuery(id+"F7.imprint","IMPRINT",FACE,{"disambiguationData":[TD([[makeQuery(id+"F7.imprint","IMPRINT",EDGE,{"derivedFrom":sQuery(id+"F7.wireOp",EDGE,"E36.sketch_text.stroke-18")}),-1.0]])]});
            var Q2;
            Q2=makeQuery(id+"F7.imprint","IMPRINT",FACE,{"disambiguationData":[TD([[makeQuery(id+"F7.imprint","IMPRINT",EDGE,{"derivedFrom":sQuery(id+"F7.wireOp",EDGE,"E36.sketch_text.stroke-38")}),-1.0]])]});
            var Q3;
            Q3=makeQuery(id+"F7.imprint","IMPRINT",FACE,{"disambiguationData":[TD([[makeQuery(id+"F7.imprint","IMPRINT",EDGE,{"derivedFrom":sQuery(id+"F7.wireOp",EDGE,"E36.sketch_text.stroke-68")}),-1.0]])]});
            var Q4;
            Q4=makeQuery(id+"F7.imprint","IMPRINT",FACE,{"disambiguationData":[TD([[makeQuery(id+"F7.imprint","IMPRINT",EDGE,{"derivedFrom":sQuery(id+"F7.wireOp",EDGE,"E36.sketch_text.stroke-98")}),-1.0]])]});
            var Q5;
            Q5=makeQuery(id+"F7.imprint","IMPRINT",FACE,{"disambiguationData":[TD([[makeQuery(id+"F7.imprint","IMPRINT",EDGE,{"derivedFrom":sQuery(id+"F7.wireOp",EDGE,"E36.sketch_text.stroke-110")}),-1.0]])]});
            var Q6;
            Q6=makeQuery(id+"F7.imprint","IMPRINT",FACE,{"disambiguationData":[TD([[makeQuery(id+"F7.imprint","IMPRINT",EDGE,{"derivedFrom":sQuery(id+"F7.wireOp",EDGE,"E36.sketch_text.stroke-126")}),-1.0]])]});
            var Q7;
            Q7=makeQuery(id+"F7.imprint","IMPRINT",FACE,{"disambiguationData":[TD([[makeQuery(id+"F7.imprint","IMPRINT",EDGE,{"derivedFrom":sQuery(id+"F7.wireOp",EDGE,"E36.sketch_text.stroke-156")}),-1.0]])]});
            var Q8;
            Q8=makeQuery(id+"F7.imprint","IMPRINT",FACE,{"disambiguationData":[TD([[makeQuery(id+"F7.imprint","IMPRINT",EDGE,{"derivedFrom":sQuery(id+"F7.wireOp",EDGE,"E36.sketch_text.stroke-168")}),-1.0]])]});
            var Q9;
            Q9=makeQuery(id+"F7.imprint","IMPRINT",FACE,{"disambiguationData":[TD([[makeQuery(id+"F7.imprint","IMPRINT",EDGE,{"derivedFrom":sQuery(id+"F7.wireOp",EDGE,"E36.sketch_text.stroke-192")}),-1.0]])]});
            var Q10;
            {var subQ0=sQuery(id+"F7.wireOp",EDGE,"E20");var subQ1=sQuery(id+"F7.wireOp",EDGE,"E16.bottom");var subQ2=makeQuery(id+"F7.imprint","INTERSECT",VERTEX,{"disambiguationData":[OD(0.0)],"derivedFrom":[subQ1,subQ0]});Q10=makeQuery(id+"F7.imprint","IMPRINT",FACE,{"disambiguationData":[TD([[makeQuery(id+"F7.imprint","IMPRINT",EDGE,{"disambiguationData":[TD([[subQ2,-1.0]])],"derivedFrom":subQ1}),1.0]])]});}
            var Q11;
            {var subQ0=sQuery(id+"F7.wireOp",EDGE,"E20");var subQ1=sQuery(id+"F7.wireOp",EDGE,"E16.bottom");var subQ2=makeQuery(id+"F7.imprint","INTERSECT",VERTEX,{"disambiguationData":[OD(0.0)],"derivedFrom":[subQ1,subQ0]});Q11=makeQuery(id+"F7.imprint","IMPRINT",FACE,{"disambiguationData":[TD([[makeQuery(id+"F7.imprint","IMPRINT",EDGE,{"disambiguationData":[TD([[subQ2,-1.0]])],"derivedFrom":subQ1}),-1.0]])]});}
            var Q12;
            {var subQ0=sQuery(id+"F7.wireOp",EDGE,"E20");var subQ1=sQuery(id+"F7.wireOp",EDGE,"E16.top");var subQ2=makeQuery(id+"F7.imprint","INTERSECT",VERTEX,{"disambiguationData":[OD(0.0)],"derivedFrom":[subQ1,subQ0]});Q12=makeQuery(id+"F7.imprint","IMPRINT",FACE,{"disambiguationData":[TD([[makeQuery(id+"F7.imprint","IMPRINT",EDGE,{"disambiguationData":[TD([[subQ2,-1.0]])],"derivedFrom":subQ1}),-1.0]])]});}
            var Q13;
            {var subQ0=sQuery(id+"F7.wireOp",EDGE,"E20");var subQ1=sQuery(id+"F7.wireOp",EDGE,"E17.bottom");var subQ2=makeQuery(id+"F7.imprint","INTERSECT",VERTEX,{"disambiguationData":[OD(0.0)],"derivedFrom":[subQ1,subQ0]});Q13=makeQuery(id+"F7.imprint","IMPRINT",FACE,{"disambiguationData":[TD([[makeQuery(id+"F7.imprint","IMPRINT",EDGE,{"disambiguationData":[TD([[subQ2,-1.0]])],"derivedFrom":subQ1}),-1.0]])]});}
            var Q14;
            {var subQ0=sQuery(id+"F7.wireOp",EDGE,"E20");var subQ1=sQuery(id+"F7.wireOp",EDGE,"E17.top");var subQ2=makeQuery(id+"F7.imprint","INTERSECT",VERTEX,{"disambiguationData":[OD(0.0)],"derivedFrom":[subQ1,subQ0]});Q14=makeQuery(id+"F7.imprint","IMPRINT",FACE,{"disambiguationData":[TD([[makeQuery(id+"F7.imprint","IMPRINT",EDGE,{"disambiguationData":[TD([[subQ2,-1.0]])],"derivedFrom":subQ1}),-1.0]])]});}
            var Q15;
            {var subQ0=sQuery(id+"F7.wireOp",EDGE,"E17.right");Q15=makeQuery(id+"F7.imprint","IMPRINT",FACE,{"disambiguationData":[TD([[makeQuery(id+"F7.imprint","IMPRINT",EDGE,{"derivedFrom":subQ0}),-1.0]])]});}
            var Q16;
            {var subQ0=sQuery(id+"F7.wireOp",EDGE,"E16.right");Q16=makeQuery(id+"F7.imprint","IMPRINT",FACE,{"disambiguationData":[TD([[makeQuery(id+"F7.imprint","IMPRINT",EDGE,{"derivedFrom":subQ0}),-1.0]])]});}
            var Q17;
            {var subQ0=sQuery(id+"F7.wireOp",EDGE,"E19");var subQ1=sQuery(id+"F7.wireOp",EDGE,"E16.bottom");var subQ2=makeQuery(id+"F7.imprint","INTERSECT",VERTEX,{"disambiguationData":[OD(1.0)],"derivedFrom":[subQ1,subQ0]});Q17=makeQuery(id+"F7.imprint","IMPRINT",FACE,{"disambiguationData":[TD([[makeQuery(id+"F7.imprint","IMPRINT",EDGE,{"disambiguationData":[TD([[subQ2,-1.0]])],"derivedFrom":subQ1}),-1.0]])]});}
            var Q18;
            {var subQ0=sQuery(id+"F7.wireOp",EDGE,"E19");var subQ1=sQuery(id+"F7.wireOp",EDGE,"E17.bottom");var subQ2=makeQuery(id+"F7.imprint","INTERSECT",VERTEX,{"disambiguationData":[OD(1.0)],"derivedFrom":[subQ1,subQ0]});Q18=makeQuery(id+"F7.imprint","IMPRINT",FACE,{"disambiguationData":[TD([[makeQuery(id+"F7.imprint","IMPRINT",EDGE,{"disambiguationData":[TD([[subQ2,-1.0]])],"derivedFrom":subQ1}),-1.0]])]});}
            var Q19;
            {var subQ0=sQuery(id+"F7.wireOp",EDGE,"E19");var subQ1=sQuery(id+"F7.wireOp",EDGE,"E16.bottom");var subQ2=makeQuery(id+"F7.imprint","INTERSECT",VERTEX,{"disambiguationData":[OD(0.0)],"derivedFrom":[subQ1,subQ0]});Q19=makeQuery(id+"F7.imprint","IMPRINT",FACE,{"disambiguationData":[TD([[makeQuery(id+"F7.imprint","IMPRINT",EDGE,{"disambiguationData":[TD([[subQ2,-1.0]])],"derivedFrom":subQ1}),-1.0]])]});}
            var Q20;
            {var subQ0=sQuery(id+"F7.wireOp",EDGE,"E19");var subQ1=sQuery(id+"F7.wireOp",EDGE,"E16.top");var subQ2=makeQuery(id+"F7.imprint","INTERSECT",VERTEX,{"disambiguationData":[OD(0.0)],"derivedFrom":[subQ1,subQ0]});Q20=makeQuery(id+"F7.imprint","IMPRINT",FACE,{"disambiguationData":[TD([[makeQuery(id+"F7.imprint","IMPRINT",EDGE,{"disambiguationData":[TD([[subQ2,-1.0]])],"derivedFrom":subQ1}),-1.0]])]});}
            var Q21;
            {var subQ0=sQuery(id+"F7.wireOp",EDGE,"E19");var subQ1=sQuery(id+"F7.wireOp",EDGE,"E17.bottom");var subQ2=makeQuery(id+"F7.imprint","INTERSECT",VERTEX,{"disambiguationData":[OD(0.0)],"derivedFrom":[subQ1,subQ0]});Q21=makeQuery(id+"F7.imprint","IMPRINT",FACE,{"disambiguationData":[TD([[makeQuery(id+"F7.imprint","IMPRINT",EDGE,{"disambiguationData":[TD([[subQ2,-1.0]])],"derivedFrom":subQ1}),-1.0]])]});}
            var Q22;
            {var subQ0=sQuery(id+"F7.wireOp",EDGE,"E17.left");Q22=makeQuery(id+"F7.imprint","IMPRINT",FACE,{"disambiguationData":[TD([[makeQuery(id+"F7.imprint","IMPRINT",EDGE,{"derivedFrom":subQ0}),1.0]])]});}
            var Q23;
            {var subQ0=sQuery(id+"F7.wireOp",EDGE,"E16.left");Q23=makeQuery(id+"F7.imprint","IMPRINT",FACE,{"disambiguationData":[TD([[makeQuery(id+"F7.imprint","IMPRINT",EDGE,{"derivedFrom":subQ0}),1.0]])]});}
            var Q24;
            {var subQ0=sQuery(id+"F7.wireOp",EDGE,"E19");var subQ1=sQuery(id+"F7.wireOp",EDGE,"E16.bottom");var subQ2=makeQuery(id+"F7.imprint","INTERSECT",VERTEX,{"disambiguationData":[OD(0.0)],"derivedFrom":[subQ1,subQ0]});Q24=makeQuery(id+"F7.imprint","IMPRINT",FACE,{"disambiguationData":[TD([[makeQuery(id+"F7.imprint","IMPRINT",EDGE,{"disambiguationData":[TD([[subQ2,-1.0]])],"derivedFrom":subQ1}),1.0]])]});}
            var Q25;
            {var subQ0=sQuery(id+"F7.wireOp",EDGE,"E19");var subQ1=sQuery(id+"F7.wireOp",EDGE,"E17.top");var subQ2=makeQuery(id+"F7.imprint","INTERSECT",VERTEX,{"disambiguationData":[OD(0.0)],"derivedFrom":[subQ1,subQ0]});Q25=makeQuery(id+"F7.imprint","IMPRINT",FACE,{"disambiguationData":[TD([[makeQuery(id+"F7.imprint","IMPRINT",EDGE,{"disambiguationData":[TD([[subQ2,-1.0]])],"derivedFrom":subQ1}),-1.0]])]});}
            var Q26;
            {var subQ0=sQuery(id+"F7.wireOp",EDGE,"E19");var subQ1=sQuery(id+"F7.wireOp",EDGE,"E18");var subQ2=makeQuery(id+"F7.imprint","INTERSECT",VERTEX,{"disambiguationData":[OD(0.0)],"derivedFrom":[subQ1,subQ0]});Q26=makeQuery(id+"F7.imprint","IMPRINT",FACE,{"disambiguationData":[TD([[makeQuery(id+"F7.imprint","IMPRINT",EDGE,{"disambiguationData":[TD([[subQ2,1.0]])],"derivedFrom":subQ1}),1.0]])]});}
            var Q27;
            {var subQ0=sQuery(id+"F7.wireOp",EDGE,"E19");var subQ1=sQuery(id+"F7.wireOp",EDGE,"E18");var subQ2=makeQuery(id+"F7.imprint","INTERSECT",VERTEX,{"disambiguationData":[OD(1.0)],"derivedFrom":[subQ1,subQ0]});Q27=makeQuery(id+"F7.imprint","IMPRINT",FACE,{"disambiguationData":[TD([[makeQuery(id+"F7.imprint","IMPRINT",EDGE,{"disambiguationData":[TD([[subQ2,1.0]])],"derivedFrom":subQ1}),1.0]])]});}
            var Q28;
            {var subQ0=sQuery(id+"F7.wireOp",EDGE,"E19");var subQ1=sQuery(id+"F7.wireOp",EDGE,"E18");var subQ2=makeQuery(id+"F7.imprint","INTERSECT",VERTEX,{"disambiguationData":[OD(0.0)],"derivedFrom":[subQ1,subQ0]});Q28=makeQuery(id+"F7.imprint","IMPRINT",FACE,{"disambiguationData":[TD([[makeQuery(id+"F7.imprint","IMPRINT",EDGE,{"disambiguationData":[TD([[subQ2,-1.0]])],"derivedFrom":subQ1}),1.0]])]});}
            var Q29;
            {var subQ0=sQuery(id+"F7.wireOp",EDGE,"E19");var subQ1=sQuery(id+"F7.wireOp",EDGE,"E18");var subQ2=makeQuery(id+"F7.imprint","INTERSECT",VERTEX,{"disambiguationData":[OD(2.0)],"derivedFrom":[subQ1,subQ0]});Q29=makeQuery(id+"F7.imprint","IMPRINT",FACE,{"disambiguationData":[TD([[makeQuery(id+"F7.imprint","IMPRINT",EDGE,{"disambiguationData":[TD([[subQ2,-1.0]])],"derivedFrom":subQ1}),1.0]])]});}
            var Q30;
            {var subQ0=sQuery(id+"F7.wireOp",EDGE,"E19");var subQ1=sQuery(id+"F7.wireOp",EDGE,"E18");var subQ2=makeQuery(id+"F7.imprint","INTERSECT",VERTEX,{"disambiguationData":[OD(4.0)],"derivedFrom":[subQ1,subQ0]});Q30=makeQuery(id+"F7.imprint","IMPRINT",FACE,{"disambiguationData":[TD([[makeQuery(id+"F7.imprint","IMPRINT",EDGE,{"disambiguationData":[TD([[subQ2,-1.0]])],"derivedFrom":subQ1}),-1.0]])]});}
            var Q31;
            {var subQ0=sQuery(id+"F7.wireOp",EDGE,"E19");var subQ1=sQuery(id+"F7.wireOp",EDGE,"E18");var subQ2=makeQuery(id+"F7.imprint","INTERSECT",VERTEX,{"disambiguationData":[OD(3.0)],"derivedFrom":[subQ1,subQ0]});Q31=makeQuery(id+"F7.imprint","IMPRINT",FACE,{"disambiguationData":[TD([[makeQuery(id+"F7.imprint","IMPRINT",EDGE,{"disambiguationData":[TD([[subQ2,-1.0]])],"derivedFrom":subQ1}),1.0]])]});}
            var Q32;
            {var subQ0=sQuery(id+"F7.wireOp",EDGE,"E19");var subQ1=sQuery(id+"F7.wireOp",EDGE,"E18");var subQ2=makeQuery(id+"F7.imprint","INTERSECT",VERTEX,{"disambiguationData":[OD(2.0)],"derivedFrom":[subQ1,subQ0]});Q32=makeQuery(id+"F7.imprint","IMPRINT",FACE,{"disambiguationData":[TD([[makeQuery(id+"F7.imprint","IMPRINT",EDGE,{"disambiguationData":[TD([[subQ2,-1.0]])],"derivedFrom":subQ1}),-1.0]])]});}
            extrude(context, id + "F8", {"entities" : qUnion([Q0, Q1, Q2, Q3, Q4, Q5, Q6, Q7, Q8, Q9, Q10, Q11, Q12, Q13, Q14, Q15, Q16, Q17, Q18, Q19, Q20, Q21, Q22, Q23, Q24, Q25, Q26, Q27, Q28, Q29, Q30, Q31, Q32]), "operationType" : NewBodyOperationType.REMOVE, "oppositeDirection" : true, "depth" : 0.76 * mm, "offsetDistance" : 25.4 * mm});
        }
        {
            var Q0;
            {var subQ0=sQuery(id+"F7.wireOp",EDGE,"E22");var subQ1=sQuery(id+"F7.wireOp",EDGE,"E21");var subQ2=makeQuery(id+"F7.imprint","INTERSECT",VERTEX,{"disambiguationData":[OD(0.0)],"derivedFrom":[subQ1,subQ0]});Q0=makeQuery(id+"F7.imprint","IMPRINT",FACE,{"disambiguationData":[TD([[makeQuery(id+"F7.imprint","IMPRINT",EDGE,{"disambiguationData":[TD([[subQ2,-1.0]])],"derivedFrom":subQ1}),-1.0]])]});}
            var Q1;
            {var subQ0=sQuery(id+"F7.wireOp",EDGE,"E22");var subQ1=sQuery(id+"F7.wireOp",EDGE,"E21");var subQ2=makeQuery(id+"F7.imprint","INTERSECT",VERTEX,{"disambiguationData":[OD(0.0)],"derivedFrom":[subQ1,subQ0]});Q1=makeQuery(id+"F7.imprint","IMPRINT",FACE,{"disambiguationData":[TD([[makeQuery(id+"F7.imprint","IMPRINT",EDGE,{"disambiguationData":[TD([[subQ2,1.0]])],"derivedFrom":subQ1}),-1.0]])]});}
            var Q2;
            {var subQ0=sQuery(id+"F7.wireOp",EDGE,"E22");var subQ1=sQuery(id+"F7.wireOp",EDGE,"E21");var subQ2=makeQuery(id+"F7.imprint","INTERSECT",VERTEX,{"disambiguationData":[OD(0.0)],"derivedFrom":[subQ1,subQ0]});Q2=makeQuery(id+"F7.imprint","IMPRINT",FACE,{"disambiguationData":[TD([[makeQuery(id+"F7.imprint","IMPRINT",EDGE,{"disambiguationData":[TD([[subQ2,1.0]])],"derivedFrom":subQ1}),1.0]])]});}
            var Q3;
            {var subQ0=sQuery(id+"F7.wireOp",EDGE,"E23");var subQ1=sQuery(id+"F7.wireOp",EDGE,"E22");var subQ2=makeQuery(id+"F7.imprint","INTERSECT",VERTEX,{"disambiguationData":[OD(0.0)],"derivedFrom":[subQ1,subQ0]});Q3=makeQuery(id+"F7.imprint","IMPRINT",FACE,{"disambiguationData":[TD([[makeQuery(id+"F7.imprint","IMPRINT",EDGE,{"disambiguationData":[TD([[subQ2,-1.0]])],"derivedFrom":subQ1}),1.0]])]});}
            var Q4;
            {var subQ0=sQuery(id+"F7.wireOp",EDGE,"E23");var subQ1=sQuery(id+"F7.wireOp",EDGE,"E22");var subQ2=makeQuery(id+"F7.imprint","INTERSECT",VERTEX,{"disambiguationData":[OD(0.0)],"derivedFrom":[subQ1,subQ0]});Q4=makeQuery(id+"F7.imprint","IMPRINT",FACE,{"disambiguationData":[TD([[makeQuery(id+"F7.imprint","IMPRINT",EDGE,{"disambiguationData":[TD([[subQ2,-1.0]])],"derivedFrom":subQ1}),-1.0]])]});}
            var Q5;
            Q5=makeQuery(id+"F7.imprint","IMPRINT",FACE,{"disambiguationData":[TD([[makeQuery(id+"F7.imprint","IMPRINT",EDGE,{"derivedFrom":sQuery(id+"F7.wireOp",EDGE,"E24")}),-1.0]])]});
            var Q6;
            {var subQ0=sQuery(id+"F7.wireOp",EDGE,"E26");var subQ1=sQuery(id+"F7.wireOp",EDGE,"E23");var subQ2=makeQuery(id+"F7.imprint","INTERSECT",VERTEX,{"disambiguationData":[OD(0.0)],"derivedFrom":[subQ1,subQ0]});Q6=makeQuery(id+"F7.imprint","IMPRINT",FACE,{"disambiguationData":[TD([[makeQuery(id+"F7.imprint","IMPRINT",EDGE,{"disambiguationData":[TD([[subQ2,-1.0]])],"derivedFrom":subQ1}),1.0]])]});}
            var Q7;
            Q7=makeQuery(id+"F7.imprint","IMPRINT",FACE,{"disambiguationData":[TD([[makeQuery(id+"F7.imprint","IMPRINT",EDGE,{"derivedFrom":sQuery(id+"F7.wireOp",EDGE,"E25")}),1.0]])]});
            var Q8;
            {var subQ0=sQuery(id+"F7.wireOp",EDGE,"E27");var subQ1=sQuery(id+"F7.wireOp",EDGE,"E26");var subQ2=makeQuery(id+"F7.imprint","INTERSECT",VERTEX,{"disambiguationData":[OD(0.0)],"derivedFrom":[subQ1,subQ0]});Q8=makeQuery(id+"F7.imprint","IMPRINT",FACE,{"disambiguationData":[TD([[makeQuery(id+"F7.imprint","IMPRINT",EDGE,{"disambiguationData":[TD([[subQ2,-1.0]])],"derivedFrom":subQ1}),1.0]])]});}
            var Q9;
            {var subQ0=sQuery(id+"F7.wireOp",EDGE,"E27");var subQ1=sQuery(id+"F7.wireOp",EDGE,"E26");var subQ2=makeQuery(id+"F7.imprint","INTERSECT",VERTEX,{"disambiguationData":[OD(0.0)],"derivedFrom":[subQ1,subQ0]});Q9=makeQuery(id+"F7.imprint","IMPRINT",FACE,{"disambiguationData":[TD([[makeQuery(id+"F7.imprint","IMPRINT",EDGE,{"disambiguationData":[TD([[subQ2,-1.0]])],"derivedFrom":subQ1}),-1.0]])]});}
            var Q10;
            {var subQ0=sQuery(id+"F7.wireOp",EDGE,"E28");var subQ1=sQuery(id+"F7.wireOp",EDGE,"E27");var subQ2=makeQuery(id+"F7.imprint","INTERSECT",VERTEX,{"disambiguationData":[OD(0.0)],"derivedFrom":[subQ1,subQ0]});Q10=makeQuery(id+"F7.imprint","IMPRINT",FACE,{"disambiguationData":[TD([[makeQuery(id+"F7.imprint","IMPRINT",EDGE,{"disambiguationData":[TD([[subQ2,-1.0]])],"derivedFrom":subQ1}),1.0]])]});}
            var Q11;
            {var subQ0=sQuery(id+"F7.wireOp",EDGE,"E28");var subQ1=sQuery(id+"F7.wireOp",EDGE,"E27");var subQ2=makeQuery(id+"F7.imprint","INTERSECT",VERTEX,{"disambiguationData":[OD(0.0)],"derivedFrom":[subQ1,subQ0]});Q11=makeQuery(id+"F7.imprint","IMPRINT",FACE,{"disambiguationData":[TD([[makeQuery(id+"F7.imprint","IMPRINT",EDGE,{"disambiguationData":[TD([[subQ2,-1.0]])],"derivedFrom":subQ1}),-1.0]])]});}
            var Q12;
            {var subQ0=sQuery(id+"F7.wireOp",EDGE,"E29");var subQ1=sQuery(id+"F7.wireOp",EDGE,"E28");var subQ2=makeQuery(id+"F7.imprint","INTERSECT",VERTEX,{"disambiguationData":[OD(0.0)],"derivedFrom":[subQ1,subQ0]});Q12=makeQuery(id+"F7.imprint","IMPRINT",FACE,{"disambiguationData":[TD([[makeQuery(id+"F7.imprint","IMPRINT",EDGE,{"disambiguationData":[TD([[subQ2,1.0]])],"derivedFrom":subQ1}),-1.0]])]});}
            var Q13;
            {var subQ0=sQuery(id+"F7.wireOp",EDGE,"E29");var subQ1=sQuery(id+"F7.wireOp",EDGE,"E28");var subQ2=makeQuery(id+"F7.imprint","INTERSECT",VERTEX,{"disambiguationData":[OD(2.0)],"derivedFrom":[subQ1,subQ0]});Q13=makeQuery(id+"F7.imprint","IMPRINT",FACE,{"disambiguationData":[TD([[makeQuery(id+"F7.imprint","IMPRINT",EDGE,{"disambiguationData":[TD([[subQ2,-1.0]])],"derivedFrom":subQ1}),1.0]])]});}
            var Q14;
            {var subQ0=sQuery(id+"F7.wireOp",EDGE,"E29");var subQ1=sQuery(id+"F7.wireOp",EDGE,"E28");var subQ2=makeQuery(id+"F7.imprint","INTERSECT",VERTEX,{"disambiguationData":[OD(1.0)],"derivedFrom":[subQ1,subQ0]});Q14=makeQuery(id+"F7.imprint","IMPRINT",FACE,{"disambiguationData":[TD([[makeQuery(id+"F7.imprint","IMPRINT",EDGE,{"disambiguationData":[TD([[subQ2,1.0]])],"derivedFrom":subQ1}),-1.0]])]});}
            var Q15;
            {var subQ0=sQuery(id+"F7.wireOp",EDGE,"E29");var subQ1=sQuery(id+"F7.wireOp",EDGE,"E28");var subQ2=makeQuery(id+"F7.imprint","INTERSECT",VERTEX,{"disambiguationData":[OD(0.0)],"derivedFrom":[subQ1,subQ0]});Q15=makeQuery(id+"F7.imprint","IMPRINT",FACE,{"disambiguationData":[TD([[makeQuery(id+"F7.imprint","IMPRINT",EDGE,{"disambiguationData":[TD([[subQ2,1.0]])],"derivedFrom":subQ1}),1.0]])]});}
            extrude(context, id + "F9", {"entities" : qUnion([Q0, Q1, Q2, Q3, Q4, Q5, Q6, Q7, Q8, Q9, Q10, Q11, Q12, Q13, Q14, Q15]), "operationType" : NewBodyOperationType.REMOVE, "oppositeDirection" : true, "depth" : 0.76 * mm, "offsetDistance" : 25.4 * mm});
        }
        {
            var Q0;
            Q0=makeQuery(id+"F7.imprint","IMPRINT",FACE,{"disambiguationData":[TD([[makeQuery(id+"F7.imprint","IMPRINT",EDGE,{"derivedFrom":sQuery(id+"F7.wireOp",EDGE,"E34")}),1.0]])]});
            var Q1;
            {var subQ0=sQuery(id+"F7.wireOp",EDGE,"E35");var subQ1=sQuery(id+"F7.wireOp",EDGE,"E32");var subQ2=makeQuery(id+"F7.imprint","INTERSECT",VERTEX,{"disambiguationData":[OD(0.0)],"derivedFrom":[subQ1,subQ0]});Q1=makeQuery(id+"F7.imprint","IMPRINT",FACE,{"disambiguationData":[TD([[makeQuery(id+"F7.imprint","IMPRINT",EDGE,{"disambiguationData":[TD([[subQ2,-1.0]])],"derivedFrom":subQ1}),-1.0]])]});}
            var Q2;
            {var subQ0=sQuery(id+"F7.wireOp",EDGE,"E33");var subQ1=sQuery(id+"F7.wireOp",EDGE,"E32");var subQ2=makeQuery(id+"F7.imprint","INTERSECT",VERTEX,{"disambiguationData":[OD(0.0)],"derivedFrom":[subQ1,subQ0]});Q2=makeQuery(id+"F7.imprint","IMPRINT",FACE,{"disambiguationData":[TD([[makeQuery(id+"F7.imprint","IMPRINT",EDGE,{"disambiguationData":[TD([[subQ2,-1.0]])],"derivedFrom":subQ1}),-1.0]])]});}
            var Q3;
            {var subQ0=sQuery(id+"F7.wireOp",EDGE,"E33");var subQ1=sQuery(id+"F7.wireOp",EDGE,"E32");var subQ2=makeQuery(id+"F7.imprint","INTERSECT",VERTEX,{"disambiguationData":[OD(0.0)],"derivedFrom":[subQ1,subQ0]});Q3=makeQuery(id+"F7.imprint","IMPRINT",FACE,{"disambiguationData":[TD([[makeQuery(id+"F7.imprint","IMPRINT",EDGE,{"disambiguationData":[TD([[subQ2,1.0]])],"derivedFrom":subQ1}),1.0]])]});}
            var Q4;
            {var subQ0=sQuery(id+"F7.wireOp",EDGE,"E33");var subQ1=sQuery(id+"F7.wireOp",EDGE,"E30");var subQ2=makeQuery(id+"F7.imprint","INTERSECT",VERTEX,{"disambiguationData":[OD(0.0)],"derivedFrom":[subQ1,subQ0]});Q4=makeQuery(id+"F7.imprint","IMPRINT",FACE,{"disambiguationData":[TD([[makeQuery(id+"F7.imprint","IMPRINT",EDGE,{"disambiguationData":[TD([[subQ2,-1.0]])],"derivedFrom":subQ1}),1.0]])]});}
            var Q5;
            {var subQ0=sQuery(id+"F7.wireOp",EDGE,"E33");var subQ1=sQuery(id+"F7.wireOp",EDGE,"E32");var subQ2=makeQuery(id+"F7.imprint","INTERSECT",VERTEX,{"disambiguationData":[OD(0.0)],"derivedFrom":[subQ1,subQ0]});Q5=makeQuery(id+"F7.imprint","IMPRINT",FACE,{"disambiguationData":[TD([[makeQuery(id+"F7.imprint","IMPRINT",EDGE,{"disambiguationData":[TD([[subQ2,1.0]])],"derivedFrom":subQ1}),-1.0]])]});}
            var Q6;
            {var subQ0=sQuery(id+"F7.wireOp",EDGE,"E33");var subQ1=sQuery(id+"F7.wireOp",EDGE,"E32");var subQ2=makeQuery(id+"F7.imprint","INTERSECT",VERTEX,{"disambiguationData":[OD(1.0)],"derivedFrom":[subQ1,subQ0]});Q6=makeQuery(id+"F7.imprint","IMPRINT",FACE,{"disambiguationData":[TD([[makeQuery(id+"F7.imprint","IMPRINT",EDGE,{"disambiguationData":[TD([[subQ2,1.0]])],"derivedFrom":subQ1}),-1.0]])]});}
            var Q7;
            {var subQ0=sQuery(id+"F7.wireOp",EDGE,"E33");var subQ1=sQuery(id+"F7.wireOp",EDGE,"E30");var subQ2=makeQuery(id+"F7.imprint","INTERSECT",VERTEX,{"disambiguationData":[OD(0.0)],"derivedFrom":[subQ1,subQ0]});Q7=makeQuery(id+"F7.imprint","IMPRINT",FACE,{"disambiguationData":[TD([[makeQuery(id+"F7.imprint","IMPRINT",EDGE,{"disambiguationData":[TD([[subQ2,-1.0]])],"derivedFrom":subQ1}),-1.0]])]});}
            extrude(context, id + "F10", {"entities" : qUnion([Q0, Q1, Q2, Q3, Q4, Q5, Q6, Q7]), "operationType" : NewBodyOperationType.REMOVE, "oppositeDirection" : true, "depth" : 0.76 * mm, "offsetDistance" : 25.4 * mm});
        }
        {
            var Q0;
            {var subQ0=sQuery(id+"F7.wireOp",EDGE,"E31");var subQ1=sQuery(id+"F7.wireOp",EDGE,"E30");var subQ2=makeQuery(id+"F7.imprint","INTERSECT",VERTEX,{"disambiguationData":[OD(2.0)],"derivedFrom":[subQ1,subQ0]});Q0=makeQuery(id+"F7.imprint","IMPRINT",FACE,{"disambiguationData":[TD([[makeQuery(id+"F7.imprint","IMPRINT",EDGE,{"disambiguationData":[TD([[subQ2,-1.0]])],"derivedFrom":subQ1}),1.0]])]});}
            var Q1;
            {var subQ0=sQuery(id+"F7.wireOp",EDGE,"E31");var subQ1=sQuery(id+"F7.wireOp",EDGE,"E30");var subQ2=makeQuery(id+"F7.imprint","INTERSECT",VERTEX,{"disambiguationData":[OD(2.0)],"derivedFrom":[subQ1,subQ0]});Q1=makeQuery(id+"F7.imprint","IMPRINT",FACE,{"disambiguationData":[TD([[makeQuery(id+"F7.imprint","IMPRINT",EDGE,{"disambiguationData":[TD([[subQ2,-1.0]])],"derivedFrom":subQ1}),-1.0]])]});}
            var Q2;
            {var subQ0=sQuery(id+"F7.wireOp",EDGE,"E31");var subQ1=sQuery(id+"F7.wireOp",EDGE,"E30");var subQ2=makeQuery(id+"F7.imprint","INTERSECT",VERTEX,{"disambiguationData":[OD(0.0)],"derivedFrom":[subQ1,subQ0]});Q2=makeQuery(id+"F7.imprint","IMPRINT",FACE,{"disambiguationData":[TD([[makeQuery(id+"F7.imprint","IMPRINT",EDGE,{"disambiguationData":[TD([[subQ2,-1.0]])],"derivedFrom":subQ1}),-1.0]])]});}
            var Q3;
            {var subQ0=sQuery(id+"F7.wireOp",EDGE,"E37");var subQ1=sQuery(id+"F7.wireOp",EDGE,"E31");var subQ2=makeQuery(id+"F7.imprint","INTERSECT",VERTEX,{"disambiguationData":[OD(13.0)],"derivedFrom":[subQ1,subQ0]});Q3=makeQuery(id+"F7.imprint","IMPRINT",FACE,{"disambiguationData":[TD([[makeQuery(id+"F7.imprint","IMPRINT",EDGE,{"disambiguationData":[TD([[subQ2,-1.0]])],"derivedFrom":subQ1}),-1.0]])]});}
            var Q4;
            {var subQ1=sQuery(id+"F7.wireOp",EDGE,"E31");var subQ5=sQuery(id+"F7.wireOp",EDGE,"E30");var subQ6=makeQuery(id+"F7.imprint","INTERSECT",VERTEX,{"disambiguationData":[OD(3.0)],"derivedFrom":[subQ5,subQ1]});Q4=makeQuery(id+"F7.imprint","IMPRINT",FACE,{"disambiguationData":[TD([[makeQuery(id+"F7.imprint","IMPRINT",EDGE,{"disambiguationData":[TD([[subQ6,-1.0]])],"derivedFrom":subQ1}),1.0]])]});}
            var Q5;
            {var subQ0=sQuery(id+"F7.wireOp",EDGE,"E37");var subQ1=sQuery(id+"F7.wireOp",EDGE,"E31");var subQ2=makeQuery(id+"F7.imprint","INTERSECT",VERTEX,{"disambiguationData":[OD(12.0)],"derivedFrom":[subQ1,subQ0]});Q5=makeQuery(id+"F7.imprint","IMPRINT",FACE,{"disambiguationData":[TD([[makeQuery(id+"F7.imprint","IMPRINT",EDGE,{"disambiguationData":[TD([[subQ2,-1.0]])],"derivedFrom":subQ1}),1.0]])]});}
            var Q6;
            {var subQ0=sQuery(id+"F7.wireOp",EDGE,"E37");var subQ1=sQuery(id+"F7.wireOp",EDGE,"E30");var subQ2=makeQuery(id+"F7.imprint","INTERSECT",VERTEX,{"derivedFrom":[subQ1,subQ0]});Q6=makeQuery(id+"F7.imprint","IMPRINT",FACE,{"disambiguationData":[TD([[makeQuery(id+"F7.imprint","IMPRINT",EDGE,{"disambiguationData":[TD([[subQ2,-1.0]])],"derivedFrom":subQ1}),-1.0]])]});}
            var Q7;
            {var subQ0=sQuery(id+"F7.wireOp",EDGE,"E31");var subQ1=sQuery(id+"F7.wireOp",EDGE,"E30");var subQ2=makeQuery(id+"F7.imprint","INTERSECT",VERTEX,{"disambiguationData":[OD(0.0)],"derivedFrom":[subQ1,subQ0]});Q7=makeQuery(id+"F7.imprint","IMPRINT",FACE,{"disambiguationData":[TD([[makeQuery(id+"F7.imprint","IMPRINT",EDGE,{"disambiguationData":[TD([[subQ2,1.0]])],"derivedFrom":subQ1}),-1.0]])]});}
            var Q8;
            {var subQ0=sQuery(id+"F7.wireOp",EDGE,"E31");var subQ1=sQuery(id+"F7.wireOp",EDGE,"E30");var subQ2=makeQuery(id+"F7.imprint","INTERSECT",VERTEX,{"disambiguationData":[OD(1.0)],"derivedFrom":[subQ1,subQ0]});Q8=makeQuery(id+"F7.imprint","IMPRINT",FACE,{"disambiguationData":[TD([[makeQuery(id+"F7.imprint","IMPRINT",EDGE,{"disambiguationData":[TD([[subQ2,1.0]])],"derivedFrom":subQ1}),-1.0]])]});}
            var Q9;
            {var subQ0=sQuery(id+"F7.wireOp",EDGE,"E31");var subQ1=sQuery(id+"F7.wireOp",EDGE,"E30");var subQ2=makeQuery(id+"F7.imprint","INTERSECT",VERTEX,{"disambiguationData":[OD(0.0)],"derivedFrom":[subQ1,subQ0]});Q9=makeQuery(id+"F7.imprint","IMPRINT",FACE,{"disambiguationData":[TD([[makeQuery(id+"F7.imprint","IMPRINT",EDGE,{"disambiguationData":[TD([[subQ2,1.0]])],"derivedFrom":subQ1}),1.0]])]});}
            extrude(context, id + "F11", {"entities" : qUnion([Q0, Q1, Q2, Q3, Q4, Q5, Q6, Q7, Q8, Q9]), "operationType" : NewBodyOperationType.REMOVE, "oppositeDirection" : true, "depth" : 0.76 * mm, "offsetDistance" : 25.4 * mm});
        }
    });
